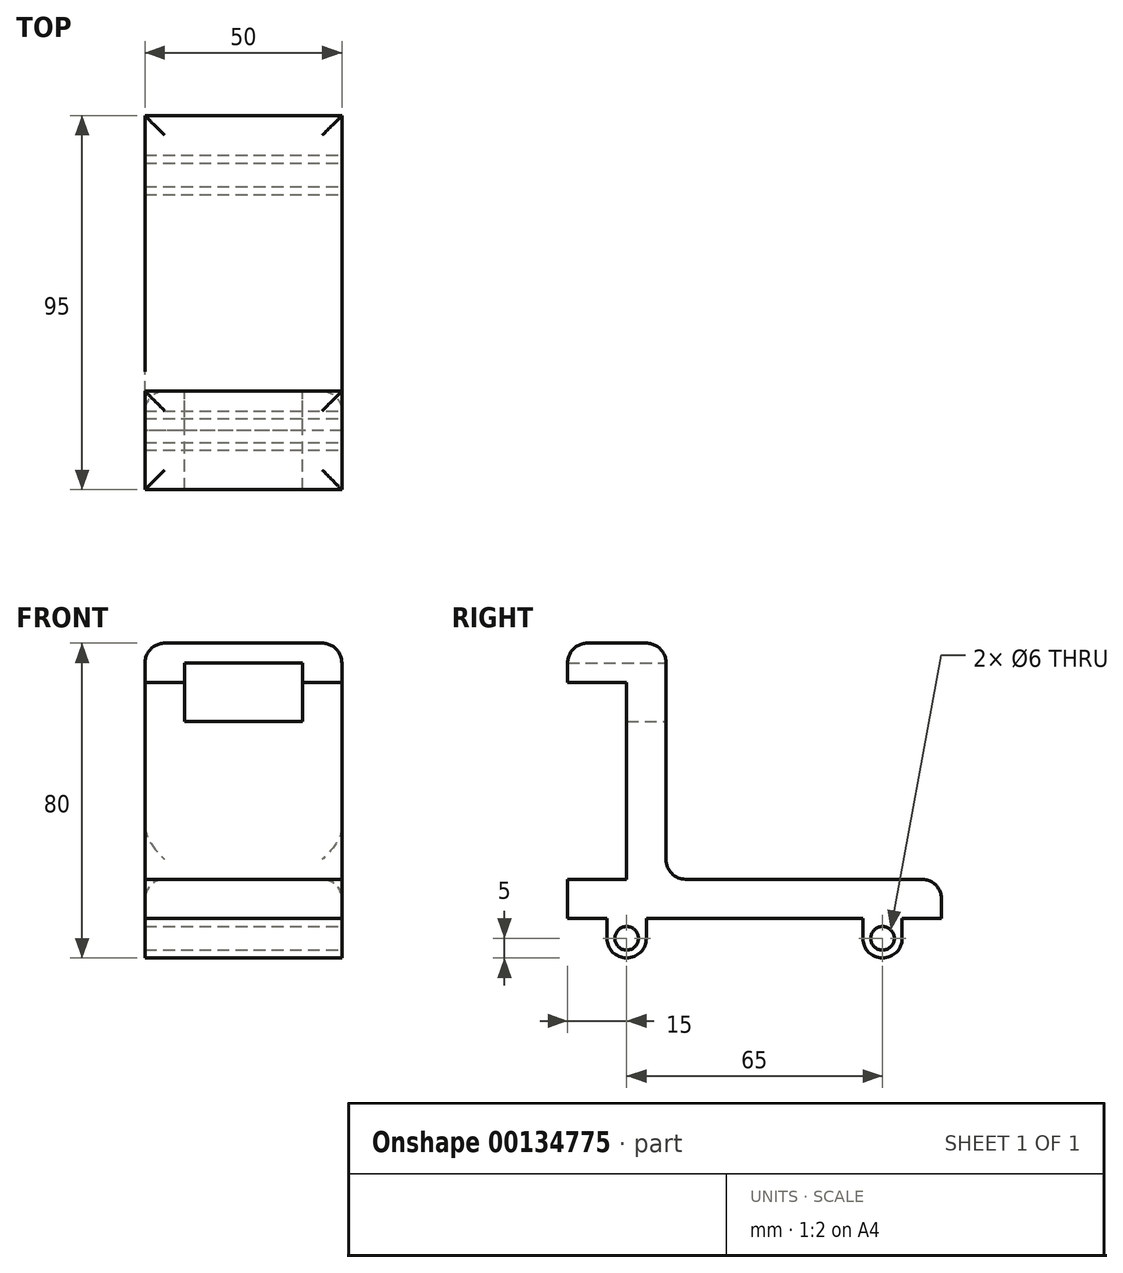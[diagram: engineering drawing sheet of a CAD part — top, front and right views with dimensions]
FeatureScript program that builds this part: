
annotation { "Feature Type Name" : "Feature", "Feature Type Description" : "" }
export const myFeature = defineFeature(function(context is Context, id is Id, definition is map)
    precondition{}
    {
        {
            var Q0;
            Q0=qCreatedBy(makeId("Right.planeOp"),FACE);
            var sketch = newSketch(context, id + "F0", { "sketchPlane" : qUnion([Q0])});
            skLineSegment(sketch, "E0", {"start": v(0, 0) * mm, "end": v(0, 10) * mm});
            skLineSegment(sketch, "E1", {"start": v(0, 10) * mm, "end": v(-70, 10) * mm});
            skLineSegment(sketch, "E2", {"start": v(-70, 10) * mm, "end": v(-70, 70) * mm});
            skLineSegment(sketch, "E3", {"start": v(-70, 70) * mm, "end": v(-82.78, 70) * mm});
            skLineSegment(sketch, "E4", {"start": v(-82.78, 70) * mm, "end": v(-95, 70) * mm});
            skLineSegment(sketch, "E5", {"start": v(-95, 70) * mm, "end": v(-95, 60) * mm});
            skLineSegment(sketch, "E6", {"start": v(-95, 60) * mm, "end": v(-80, 60) * mm});
            skLineSegment(sketch, "E7", {"start": v(-80, 60) * mm, "end": v(-80, 10) * mm});
            skLineSegment(sketch, "E8", {"start": v(-80, 10) * mm, "end": v(-95, 10) * mm});
            skLineSegment(sketch, "E9", {"start": v(-95, 10) * mm, "end": v(-95, 0) * mm});
            skLineSegment(sketch, "E10", {"start": v(-95, 0) * mm, "end": v(0, 0) * mm});
            skSolve(sketch);
        }
        {
            var Q0;
            Q0=makeQuery(id+"F0.imprint","IMPRINT",FACE,{"disambiguationData":[TD([[makeQuery(id+"F0.imprint","IMPRINT",EDGE,{"derivedFrom":sQuery(id+"F0.wireOp",EDGE,"E0")}),1.0]])]});
            extrude(context, id + "F1", {"entities" : qUnion([Q0]), "depth" : 50 * mm});
        }
        {
            var Q0;
            Q0=makeQuery(id+"F1.opExtrude","SWEPT_EDGE",EDGE,{"disambiguationData":[OSD([sQuery(id+"F0.wireOp",EDGE,"E2"),sQuery(id+"F0.wireOp",EDGE,"E3")])]});
            var Q1;
            Q1=makeQuery(id+"F1.opExtrude","CAP_EDGE",EDGE,{"disambiguationData":[OSD([sQuery(id+"F0.wireOp",EDGE,"E3"),sQuery(id+"F0.wireOp",EDGE,"E4")])],"isStart":false});
            var Q2;
            Q2=makeQuery(id+"F1.opExtrude","CAP_EDGE",EDGE,{"disambiguationData":[OSD([sQuery(id+"F0.wireOp",EDGE,"E3"),sQuery(id+"F0.wireOp",EDGE,"E4")])],"isStart":true});
            var Q3;
            Q3=makeQuery(id+"F1.opExtrude","SWEPT_EDGE",EDGE,{"disambiguationData":[OSD([sQuery(id+"F0.wireOp",EDGE,"E0"),sQuery(id+"F0.wireOp",EDGE,"E1")])]});
            var Q4;
            Q4=makeQuery(id+"F1.opExtrude","CAP_EDGE",EDGE,{"disambiguationData":[OSD([sQuery(id+"F0.wireOp",EDGE,"E1")])],"isStart":false});
            var Q5;
            Q5=makeQuery(id+"F1.opExtrude","CAP_EDGE",EDGE,{"disambiguationData":[OSD([sQuery(id+"F0.wireOp",EDGE,"E1")])],"isStart":true});
            var Q6;
            Q6=makeQuery(id+"F1.opExtrude","SWEPT_EDGE",EDGE,{"disambiguationData":[OSD([sQuery(id+"F0.wireOp",EDGE,"E1"),sQuery(id+"F0.wireOp",EDGE,"E2")])]});
            var Q7;
            Q7=makeQuery(id+"F1.opExtrude","SWEPT_EDGE",EDGE,{"disambiguationData":[OSD([sQuery(id+"F0.wireOp",EDGE,"E4"),sQuery(id+"F0.wireOp",EDGE,"E5")])]});
            fillet(context, id + "F2", {"entities" : qUnion([Q0, Q1, Q2, Q3, Q4, Q5, Q6, Q7]), "radius" : 5 * mm, "tangentPropagation" : true, "allowEdgeOverflow" : false});
        }
        {
            var Q0;
            Q0=makeQuery(id+"F1.opExtrude","CAP_FACE",FACE,{"disambiguationData":[OSD([sQuery(id+"F0.wireOp",EDGE,"E0"),sQuery(id+"F0.wireOp",EDGE,"E1"),sQuery(id+"F0.wireOp",EDGE,"E2"),sQuery(id+"F0.wireOp",EDGE,"E3"),sQuery(id+"F0.wireOp",EDGE,"E4"),sQuery(id+"F0.wireOp",EDGE,"E5"),sQuery(id+"F0.wireOp",EDGE,"E6"),sQuery(id+"F0.wireOp",EDGE,"E7"),sQuery(id+"F0.wireOp",EDGE,"E8"),sQuery(id+"F0.wireOp",EDGE,"E9"),sQuery(id+"F0.wireOp",EDGE,"E10")])],"isStart":false});
            var sketch = newSketch(context, id + "F3", { "sketchPlane" : qUnion([Q0])});
            skLineSegment(sketch, "E11.bottom", {"start": v(-85, 0) * mm, "end": v(-75, 0) * mm});
            skLineSegment(sketch, "E11.top", {"start": v(-85, -10) * mm, "end": v(-75, -10) * mm});
            skLineSegment(sketch, "E11.left", {"start": v(-85, 0) * mm, "end": v(-85, -10) * mm});
            skLineSegment(sketch, "E11.right", {"start": v(-75, 0) * mm, "end": v(-75, -10) * mm});
            skLineSegment(sketch, "E12.bottom", {"start": v(-20, 0) * mm, "end": v(-10, 0) * mm});
            skLineSegment(sketch, "E12.top", {"start": v(-20, -10) * mm, "end": v(-10, -10) * mm});
            skLineSegment(sketch, "E12.left", {"start": v(-20, 0) * mm, "end": v(-20, -10) * mm});
            skLineSegment(sketch, "E12.right", {"start": v(-10, 0) * mm, "end": v(-10, -10) * mm});
            skCircle(sketch, "E13", {"center": v(-80, -5) * mm, "radius": 3 * mm});
            skPoint(sketch, "E13.centerSnap0", {"position": v(-75, -5) * mm});
            skPoint(sketch, "E13.centerSnap1", {"position": v(-80, -10) * mm});
            skCircle(sketch, "E14", {"center": v(-15, -5) * mm, "radius": 3 * mm});
            skPoint(sketch, "E14.centerSnap0", {"position": v(-15, -10) * mm});
            skPoint(sketch, "E14.centerSnap1", {"position": v(-10, -5) * mm});
            skSolve(sketch);
        }
        {
            var Q0;
            Q0=makeQuery(id+"F3.imprint","IMPRINT",FACE,{"disambiguationData":[TD([[makeQuery(id+"F3.imprint","IMPRINT",EDGE,{"derivedFrom":sQuery(id+"F3.wireOp",EDGE,"E11.bottom")}),-1.0]])]});
            var Q1;
            Q1=makeQuery(id+"F3.imprint","IMPRINT",FACE,{"disambiguationData":[TD([[makeQuery(id+"F3.imprint","IMPRINT",EDGE,{"derivedFrom":sQuery(id+"F3.wireOp",EDGE,"E12.bottom")}),-1.0]])]});
            extrude(context, id + "F4", {"entities" : qUnion([Q0, Q1]), "operationType" : NewBodyOperationType.ADD, "oppositeDirection" : true, "depth" : 50 * mm});
        }
        {
            var Q0;
            Q0=makeQuery(id+"F4.opExtrude","SWEPT_EDGE",EDGE,{"disambiguationData":[OSD([sQuery(id+"F3.wireOp",EDGE,"E11.top"),sQuery(id+"F3.wireOp",EDGE,"E11.right")])]});
            var Q1;
            Q1=makeQuery(id+"F4.opExtrude","SWEPT_EDGE",EDGE,{"disambiguationData":[OSD([sQuery(id+"F3.wireOp",EDGE,"E11.top"),sQuery(id+"F3.wireOp",EDGE,"E11.left")])]});
            var Q2;
            Q2=makeQuery(id+"F4.opExtrude","SWEPT_EDGE",EDGE,{"disambiguationData":[OSD([sQuery(id+"F3.wireOp",EDGE,"E12.top"),sQuery(id+"F3.wireOp",EDGE,"E12.left")])]});
            var Q3;
            Q3=makeQuery(id+"F4.opExtrude","SWEPT_EDGE",EDGE,{"disambiguationData":[OSD([sQuery(id+"F3.wireOp",EDGE,"E12.top"),sQuery(id+"F3.wireOp",EDGE,"E12.right")])]});
            fillet(context, id + "F5", {"entities" : qUnion([Q0, Q1, Q2, Q3]), "radius" : 5 * mm, "tangentPropagation" : true, "allowEdgeOverflow" : false});
        }
        {
            var Q0;
            Q0=makeQuery(id+"F1.opExtrude","SWEPT_FACE",FACE,{"disambiguationData":[OSD([sQuery(id+"F0.wireOp",EDGE,"E2")])]});
            var sketch = newSketch(context, id + "F6", { "sketchPlane" : qUnion([Q0])});
            skLineSegment(sketch, "E15.bottom", {"start": v(-40, 65.04) * mm, "end": v(-10, 65.04) * mm});
            skLineSegment(sketch, "E15.top", {"start": v(-40, 50.04) * mm, "end": v(-10, 50.04) * mm});
            skLineSegment(sketch, "E15.left", {"start": v(-40, 65.04) * mm, "end": v(-40, 50.04) * mm});
            skLineSegment(sketch, "E15.right", {"start": v(-10, 65.04) * mm, "end": v(-10, 50.04) * mm});
            skSolve(sketch);
        }
        {
            var Q0;
            {var subQ0=sQuery(id+"F6.wireOp",EDGE,"E15.top");Q0=makeQuery(id+"F6.imprint","IMPRINT",FACE,{"disambiguationData":[TD([[makeQuery(id+"F6.imprint","IMPRINT",EDGE,{"derivedFrom":subQ0}),1.0]])]});}
            extrude(context, id + "F7", {"entities" : qUnion([Q0]), "operationType" : NewBodyOperationType.REMOVE, "oppositeDirection" : true, "depth" : 25 * mm});
        }
    });
